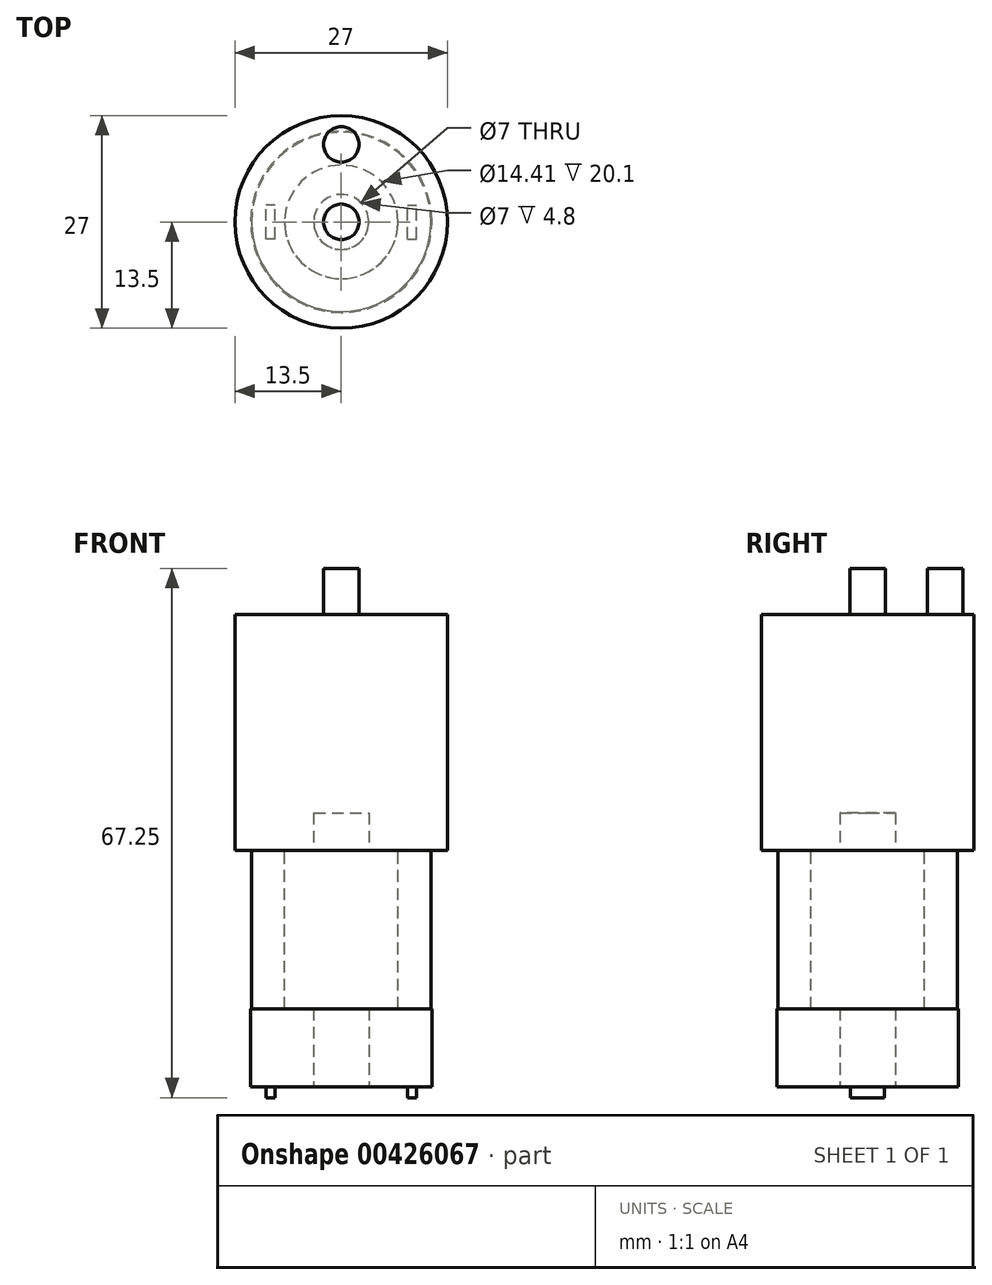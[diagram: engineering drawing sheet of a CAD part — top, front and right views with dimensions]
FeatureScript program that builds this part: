
annotation { "Feature Type Name" : "Feature", "Feature Type Description" : "" }
export const myFeature = defineFeature(function(context is Context, id is Id, definition is map)
    precondition{}
    {
        {
            var Q0;
            Q0=qCreatedBy(makeId("Right.planeOp"),FACE);
            var sketch = newSketch(context, id + "F0", { "sketchPlane" : qUnion([Q0])});
            skLineSegment(sketch, "E0", {"start": v(-11.4, 0) * mm, "end": v(-11.4, 30) * mm});
            skLineSegment(sketch, "E1", {"start": v(-11.4, 30) * mm, "end": v(-7.2, 30) * mm});
            skLineSegment(sketch, "E2", {"start": v(-7.2, 30) * mm, "end": v(-7.2, 0) * mm});
            skLineSegment(sketch, "E3", {"start": v(-7.2, 0) * mm, "end": v(-11.4, 0) * mm});
            skLineSegment(sketch, "E4", {"start": v(0, 33.61) * mm, "end": v(0, -7.5) * mm, "construction": true});
            skLineSegment(sketch, "E5", {"start": v(0, 0) * mm, "end": v(-11.4, 0) * mm, "construction": true});
            skSolve(sketch);
        }
        {
            var Q0;
            Q0=makeQuery(id+"F0.imprint","IMPRINT",FACE,{"disambiguationData":[TD([[makeQuery(id+"F0.imprint","IMPRINT",EDGE,{"derivedFrom":sQuery(id+"F0.wireOp",EDGE,"E0")}),-1.0]])]});
            var Q1;
            Q1=sQuery(id+"F0.wireOp",EDGE,"E4");
            revolve(context, id + "F1", {"entities" : qUnion([Q0]), "axis" : qUnion([Q1]), "revolveType" : RevolveType.FULL});
        }
        {
            var Q0;
            Q0=makeQuery(id+"F1.opRevolve","SWEPT_FACE",FACE,{"disambiguationData":[OSD([sQuery(id+"F0.wireOp",EDGE,"E1")])]});
            var sketch = newSketch(context, id + "F2", { "sketchPlane" : qUnion([Q0])});
            skCircle(sketch, "E6", {"center": v(0, 0) * mm, "radius": 13.5 * mm});
            skSolve(sketch);
        }
        {
            var Q0;
            Q0=qSketchRegion(id+"F2",true);
            extrude(context, id + "F3", {"entities" : qUnion([Q0]), "operationType" : NewBodyOperationType.ADD, "depth" : 30 * mm});
        }
        {
            var Q0;
            Q0=makeQuery(id+"F1.opRevolve","SWEPT_FACE",FACE,{"disambiguationData":[OSD([sQuery(id+"F0.wireOp",EDGE,"E3")])]});
            var sketch = newSketch(context, id + "F4", { "sketchPlane" : qUnion([Q0])});
            skCircle(sketch, "E7", {"center": v(0, 0) * mm, "radius": 11.5 * mm});
            skSolve(sketch);
        }
        {
            var Q0;
            Q0=qSketchRegion(id+"F4",true);
            extrude(context, id + "F5", {"entities" : qUnion([Q0]), "operationType" : NewBodyOperationType.ADD, "oppositeDirection" : true, "depth" : 9.9 * mm});
        }
        {
            var Q0;
            Q0=makeQuery(id+"F5.boolean.opBoolean","MERGE",FACE,{"derivedFrom":[makeQuery(id+"F1.opRevolve","SWEPT_FACE",FACE,{"disambiguationData":[OSD([sQuery(id+"F0.wireOp",EDGE,"E3")])]}),makeQuery(id+"F5.opExtrude","CAP_FACE",FACE,{"disambiguationData":[OSD([sQuery(id+"F4.wireOp",EDGE,"E7")])],"isStart":true})]});
            var sketch = newSketch(context, id + "F6", { "sketchPlane" : qUnion([Q0])});
            skCircle(sketch, "E8", {"center": v(0, 0) * mm, "radius": 3.5 * mm});
            skLineSegment(sketch, "E9.bottom", {"start": v(-8.42, 2.15) * mm, "end": v(-9.58, 2.15) * mm});
            skLineSegment(sketch, "E9.top", {"start": v(-8.42, -2.15) * mm, "end": v(-9.58, -2.15) * mm});
            skLineSegment(sketch, "E9.left", {"start": v(-8.42, 2.15) * mm, "end": v(-8.42, -2.15) * mm});
            skLineSegment(sketch, "E9.right", {"start": v(-9.58, 2.15) * mm, "end": v(-9.58, -2.15) * mm});
            skPoint(sketch, "E9.middle", {"position": v(-9, 0) * mm});
            skLineSegment(sketch, "E10", {"start": v(0, -12.15) * mm, "end": v(0, 12.15) * mm, "construction": true});
            skPoint(sketch, "E11.MirrorP", {"position": v(9, 0) * mm});
            skLineSegment(sketch, "E12.MirrorCS", {"start": v(9.58, 2.15) * mm, "end": v(9.58, -2.15) * mm});
            skLineSegment(sketch, "E13.MirrorCS", {"start": v(8.42, 2.15) * mm, "end": v(8.42, -2.15) * mm});
            skLineSegment(sketch, "E14.MirrorCS", {"start": v(8.42, -2.15) * mm, "end": v(9.58, -2.15) * mm});
            skLineSegment(sketch, "E15.MirrorCS", {"start": v(8.42, 2.15) * mm, "end": v(9.58, 2.15) * mm});
            skSolve(sketch);
        }
        {
            var Q0;
            Q0=makeQuery(id+"F6.imprint","IMPRINT",FACE,{"disambiguationData":[TD([[makeQuery(id+"F6.imprint","IMPRINT",EDGE,{"derivedFrom":sQuery(id+"F6.wireOp",EDGE,"E9.bottom")}),1.0]])]});
            var Q1;
            Q1=makeQuery(id+"F6.imprint","IMPRINT",FACE,{"disambiguationData":[TD([[makeQuery(id+"F6.imprint","IMPRINT",EDGE,{"derivedFrom":sQuery(id+"F6.wireOp",EDGE,"E12.MirrorCS")}),-1.0]])]});
            extrude(context, id + "F7", {"entities" : qUnion([Q0, Q1]), "operationType" : NewBodyOperationType.ADD, "depth" : 1.4 * mm});
        }
        {
            var Q0;
            Q0=makeQuery(id+"F6.imprint","IMPRINT",FACE,{"disambiguationData":[TD([[makeQuery(id+"F6.imprint","IMPRINT",EDGE,{"derivedFrom":sQuery(id+"F6.wireOp",EDGE,"E8")}),1.0]])]});
            var Q1;
            Q1=sQuery(id+"F6.wireOp",EDGE,"E8");
            extrude(context, id + "F8", {"entities" : qUnion([Q0]), "operationType" : NewBodyOperationType.REMOVE, "surfaceEntities" : qUnion([Q1]), "oppositeDirection" : true, "depth" : 34.8 * mm});
        }
        {
            var Q0;
            Q0=makeQuery(id+"F3.opExtrude","CAP_FACE",FACE,{"disambiguationData":[OSD([sQuery(id+"F2.wireOp",EDGE,"E6")])],"isStart":false});
            var sketch = newSketch(context, id + "F9", { "sketchPlane" : qUnion([Q0])});
            skCircle(sketch, "E16", {"center": v(0, 0) * mm, "radius": 2.25 * mm});
            skCircle(sketch, "E17", {"center": v(0, 9.85) * mm, "radius": 2.25 * mm});
            skLineSegment(sketch, "E18.bottom", {"start": v(13.5, 13.5) * mm, "end": v(-13.5, 13.5) * mm, "construction": true});
            skLineSegment(sketch, "E18.top", {"start": v(13.5, -13.5) * mm, "end": v(-13.5, -13.5) * mm, "construction": true});
            skLineSegment(sketch, "E18.left", {"start": v(13.5, 13.5) * mm, "end": v(13.5, -13.5) * mm, "construction": true});
            skLineSegment(sketch, "E18.right", {"start": v(-13.5, 13.5) * mm, "end": v(-13.5, -13.5) * mm, "construction": true});
            skSolve(sketch);
        }
        {
            var Q0;
            Q0=makeQuery(id+"F9.imprint","IMPRINT",FACE,{"disambiguationData":[TD([[makeQuery(id+"F9.imprint","IMPRINT",EDGE,{"derivedFrom":sQuery(id+"F9.wireOp",EDGE,"E16")}),1.0]])]});
            var Q1;
            Q1=makeQuery(id+"F9.imprint","IMPRINT",FACE,{"disambiguationData":[TD([[makeQuery(id+"F9.imprint","IMPRINT",EDGE,{"derivedFrom":sQuery(id+"F9.wireOp",EDGE,"E17")}),1.0]])]});
            extrude(context, id + "F10", {"entities" : qUnion([Q0, Q1]), "operationType" : NewBodyOperationType.ADD, "depth" : 5.85 * mm});
        }
    });
